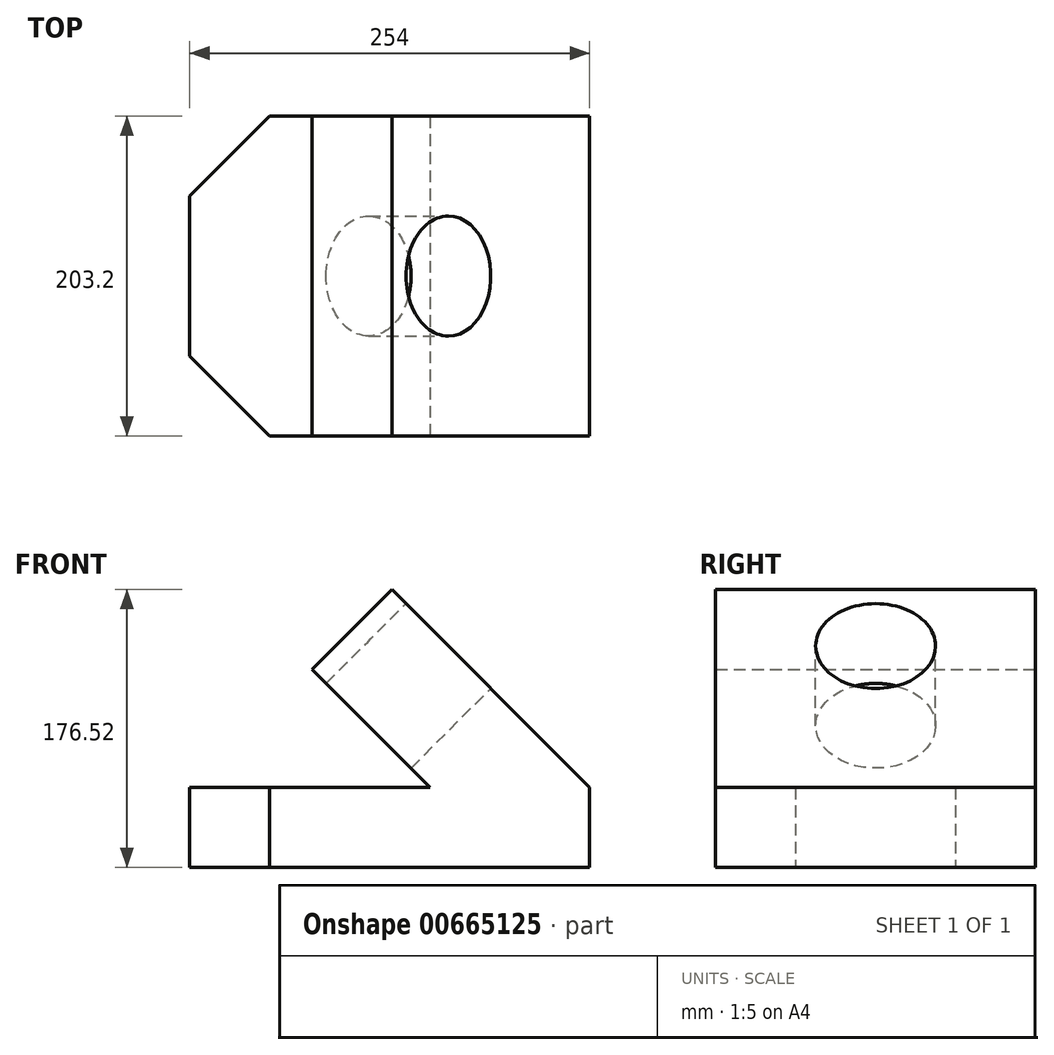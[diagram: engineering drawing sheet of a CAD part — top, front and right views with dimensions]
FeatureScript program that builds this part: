
annotation { "Feature Type Name" : "Feature", "Feature Type Description" : "" }
export const myFeature = defineFeature(function(context is Context, id is Id, definition is map)
    precondition{}
    {
        {
            var Q0;
            Q0=qCreatedBy(makeId("Top.planeOp"),FACE);
            var sketch = newSketch(context, id + "F0", { "sketchPlane" : qUnion([Q0])});
            skLineSegment(sketch, "E0", {"start": v(0, 0) * mm, "end": v(203.2, 0) * mm});
            skLineSegment(sketch, "E1", {"start": v(203.2, 0) * mm, "end": v(203.2, -203.2) * mm});
            skLineSegment(sketch, "E2", {"start": v(203.2, -203.2) * mm, "end": v(0, -203.2) * mm});
            skLineSegment(sketch, "E3", {"start": v(-50.8, -152.4) * mm, "end": v(0, -203.2) * mm});
            skLineSegment(sketch, "E4", {"start": v(-50.8, -152.4) * mm, "end": v(-50.8, -50.8) * mm});
            skLineSegment(sketch, "E5", {"start": v(-50.8, -50.8) * mm, "end": v(0, 0) * mm});
            skSolve(sketch);
        }
        {
            var Q0;
            Q0 = qSketchRegion(id + "F0", true);
            extrude(context, id + "F1", {"entities" : qUnion([Q0]), "depth" : 50.8 * mm, "offsetDistance" : 25.4 * mm});
        }
        {
            var Q0;
            Q0=qCreatedBy(makeId("Front.planeOp"),FACE);
            var sketch = newSketch(context, id + "F2", { "sketchPlane" : qUnion([Q0])});
            skLineSegment(sketch, "E6", {"start": v(0, 0) * mm, "end": v(76.2, 0) * mm});
            skLineSegment(sketch, "E7", {"start": v(76.2, 0) * mm, "end": v(76.2, 177.8) * mm});
            skLineSegment(sketch, "E8", {"start": v(0, 0) * mm, "end": v(25.4, 0) * mm});
            skLineSegment(sketch, "E9", {"start": v(25.4, 0) * mm, "end": v(25.4, 127) * mm});
            skSolve(sketch);
        }
        {
            var Q0;
            Q0=makeQuery(id+"F1.opExtrude","CAP_VERTEX",VERTEX,{"disambiguationData":[OSD([sQuery(id+"F0.wireOp",EDGE,"E1"),sQuery(id+"F0.wireOp",EDGE,"E2")])],"isStart":false});
            var Q1;
            Q1=makeQuery(id+"F1.opExtrude","CAP_VERTEX",VERTEX,{"disambiguationData":[OSD([sQuery(id+"F0.wireOp",EDGE,"E0"),sQuery(id+"F0.wireOp",EDGE,"E1")])],"isStart":false});
            var Q2;
            Q2=sQuery(id+"F2.wireOp",VERTEX,"E7.end");
            cPlane(context, id + "F3", {"entities" : qUnion([Q0, Q1, Q2]), "cplaneType" : CPlaneType.THREE_POINT, "offset" : 25.4 * mm, "width" : 152.4 * mm, "height" : 152.4 * mm});
        }
        {
            var Q0;
            Q0=qCreatedBy(id+"F3.planeOp",FACE);
            var sketch = newSketch(context, id + "F4", { "sketchPlane" : qUnion([Q0])});
            skLineSegment(sketch, "E10", {"start": v(0, 70.04) * mm, "end": v(0, -107.76) * mm});
            skLineSegment(sketch, "E11", {"start": v(0, -107.76) * mm, "end": v(203.2, -107.76) * mm});
            skLineSegment(sketch, "E12", {"start": v(203.2, -107.76) * mm, "end": v(203.2, 70.04) * mm});
            skLineSegment(sketch, "E13", {"start": v(203.2, 70.04) * mm, "end": v(0, 70.04) * mm});
            skCircle(sketch, "E14", {"center": v(101.6, 19.24) * mm, "radius": 38.1 * mm});
            skSolve(sketch);
        }
        {
            var Q0;
            Q0=makeQuery(id+"F4.imprint","IMPRINT",FACE,{"disambiguationData":[TD([[makeQuery(id+"F4.imprint","IMPRINT",EDGE,{"derivedFrom":sQuery(id+"F4.wireOp",EDGE,"E10")}),1.0]])]});
            extrude(context, id + "F5", {"entities" : qUnion([Q0]), "operationType" : NewBodyOperationType.ADD, "depth" : 71.63 * mm, "offsetDistance" : 25.4 * mm});
        }
    });
